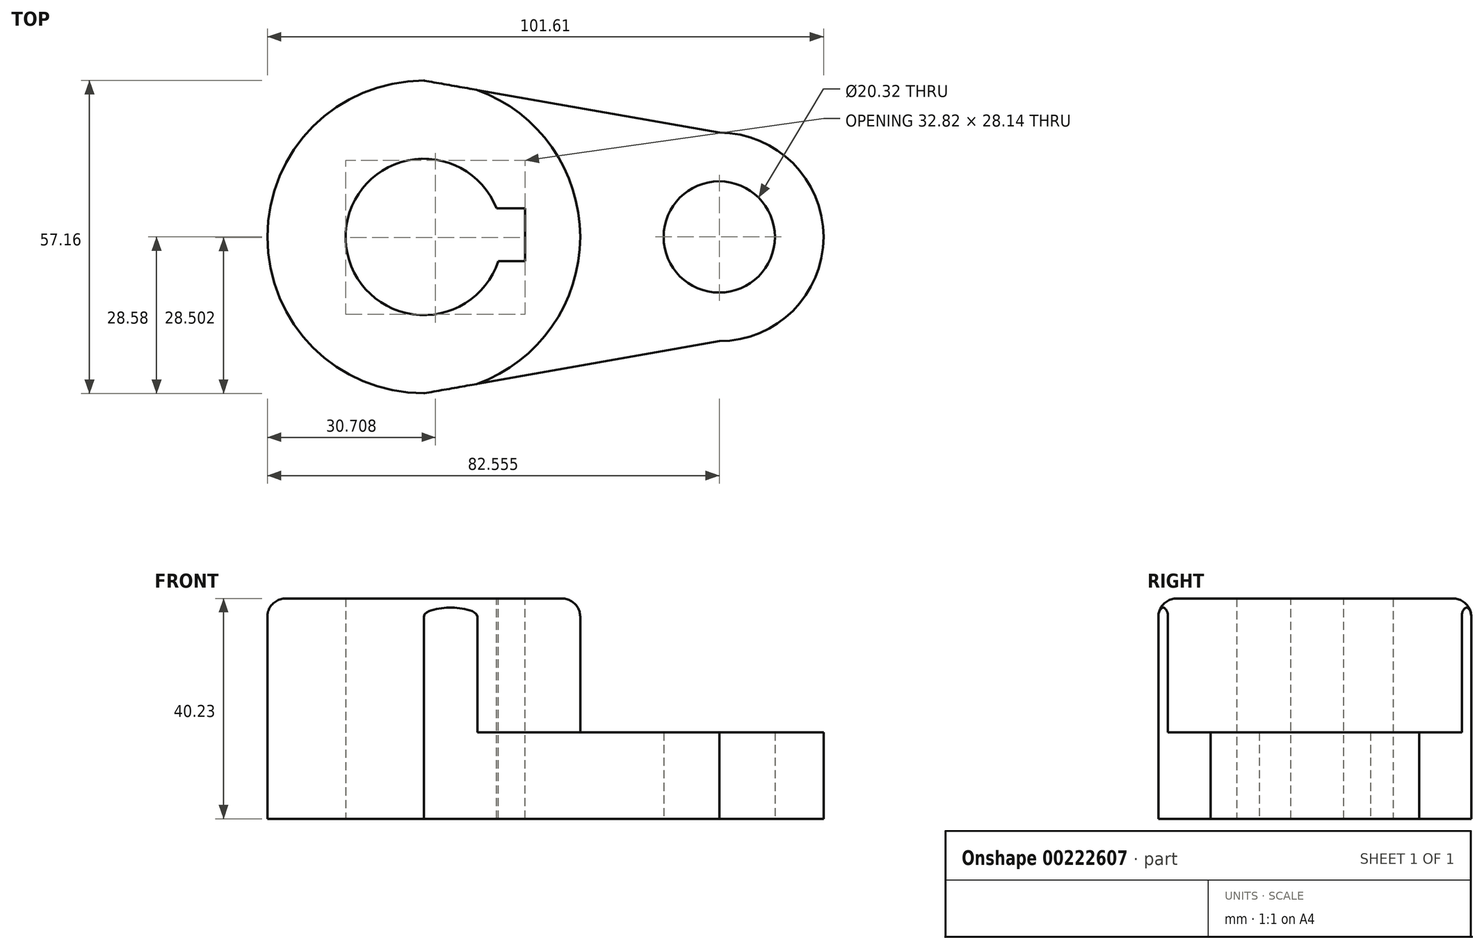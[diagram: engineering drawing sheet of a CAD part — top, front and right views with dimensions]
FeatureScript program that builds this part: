
annotation { "Feature Type Name" : "Feature", "Feature Type Description" : "" }
export const myFeature = defineFeature(function(context is Context, id is Id, definition is map)
    precondition{}
    {
        {
            var Q0;
            Q0=qCreatedBy(makeId("Top.planeOp"),FACE);
            var sketch = newSketch(context, id + "F0", { "sketchPlane" : qUnion([Q0])});
            skCircle(sketch, "E0", {"center": v(0, 0) * mm, "radius": 14.29 * mm});
            skCircle(sketch, "E1", {"center": v(53.98, 0) * mm, "radius": 10.16 * mm});
            skCircle(sketch, "E2", {"center": v(0, 0) * mm, "radius": 28.58 * mm});
            skArc(sketch, "E3", {"start": v(53.97, -19.05) * mm, "mid": v(73.03, 0) * mm, "end": v(53.98, 19.05) * mm});
            skLineSegment(sketch, "E4", {"start": v(0, 28.58) * mm, "end": v(53.98, 19.05) * mm});
            skLineSegment(sketch, "E5", {"start": v(0, -28.58) * mm, "end": v(53.97, -19.05) * mm});
            skSolve(sketch);
        }
        {
            var Q0;
            {var subQ0=sQuery(id+"F0.wireOp",EDGE,"E4");var subQ1=sQuery(id+"F0.wireOp",EDGE,"E2");var subQ2=makeQuery(id+"F0.imprint","INTERSECT",VERTEX,{"disambiguationData":[OD(0.0)],"derivedFrom":[subQ1,subQ0]});Q0=makeQuery(id+"F0.imprint","IMPRINT",FACE,{"disambiguationData":[TD([[makeQuery(id+"F0.imprint","IMPRINT",EDGE,{"disambiguationData":[TD([[subQ2,1.0]])],"derivedFrom":subQ1}),1.0]])]});}
            var Q1;
            {var subQ0=sQuery(id+"F0.wireOp",EDGE,"E5");var subQ1=sQuery(id+"F0.wireOp",EDGE,"E2");var subQ2=makeQuery(id+"F0.imprint","INTERSECT",VERTEX,{"disambiguationData":[OD(0.0)],"derivedFrom":[subQ1,subQ0]});Q1=makeQuery(id+"F0.imprint","IMPRINT",FACE,{"disambiguationData":[TD([[makeQuery(id+"F0.imprint","IMPRINT",EDGE,{"disambiguationData":[TD([[subQ2,-1.0]])],"derivedFrom":subQ1}),1.0]])]});}
            var Q2;
            Q2=makeQuery(id+"F0.imprint","IMPRINT",FACE,{"disambiguationData":[TD([[makeQuery(id+"F0.imprint","IMPRINT",EDGE,{"derivedFrom":sQuery(id+"F0.wireOp",EDGE,"E0")}),-1.0]])]});
            extrude(context, id + "F1", {"entities" : qUnion([Q0, Q1, Q2]), "depth" : 40.23 * mm});
        }
        {
            var Q0;
            Q0=makeQuery(id+"F0.imprint","IMPRINT",FACE,{"disambiguationData":[TD([[makeQuery(id+"F0.imprint","IMPRINT",EDGE,{"derivedFrom":sQuery(id+"F0.wireOp",EDGE,"E1")}),-1.0]])]});
            extrude(context, id + "F2", {"entities" : qUnion([Q0]), "operationType" : NewBodyOperationType.ADD, "depth" : 15.77 * mm});
        }
        {
            var Q0;
            Q0=makeQuery(id+"F1.opExtrude","CAP_FACE",FACE,{"disambiguationData":[OSD([sQuery(id+"F0.wireOp",EDGE,"E0"),sQuery(id+"F0.wireOp",EDGE,"E2")])],"isStart":false});
            var sketch = newSketch(context, id + "F3", { "sketchPlane" : qUnion([Q0])});
            skLineSegment(sketch, "E6", {"start": v(0, 5.25) * mm, "end": v(18.54, 5.25) * mm});
            skLineSegment(sketch, "E7", {"start": v(18.54, 5.25) * mm, "end": v(18.54, -4.4) * mm});
            skLineSegment(sketch, "E8", {"start": v(18.54, -4.4) * mm, "end": v(0, -4.4) * mm});
            skLineSegment(sketch, "E9", {"start": v(0, -4.4) * mm, "end": v(0, 5.25) * mm});
            skLineSegment(sketch, "E10", {"start": v(-14.28, 0.43) * mm, "end": v(-14.28, 30.21) * mm, "construction": true});
            skPoint(sketch, "E10.startSnap0", {"position": v(0, 0.43) * mm});
            skSolve(sketch);
        }
        {
            var Q0;
            {var subQ0=sQuery(id+"F3.wireOp",EDGE,"E7");Q0=makeQuery(id+"F3.imprint","IMPRINT",FACE,{"disambiguationData":[TD([[makeQuery(id+"F3.imprint","IMPRINT",EDGE,{"derivedFrom":subQ0}),-1.0]])]});}
            extrude(context, id + "F4", {"entities" : qUnion([Q0]), "operationType" : NewBodyOperationType.REMOVE, "endBound" : BoundingType.UP_TO_NEXT, "oppositeDirection" : true, "depth" : 25.4 * mm});
        }
        {
            var Q0;
            Q0=makeQuery(id+"F1.opExtrude","CAP_EDGE",EDGE,{"disambiguationData":[OSD([sQuery(id+"F0.wireOp",EDGE,"E2")])],"isStart":false});
            fillet(context, id + "F5", {"entities" : qUnion([Q0]), "radius" : 3.3 * mm, "tangentPropagation" : true, "allowEdgeOverflow" : false});
        }
    });
